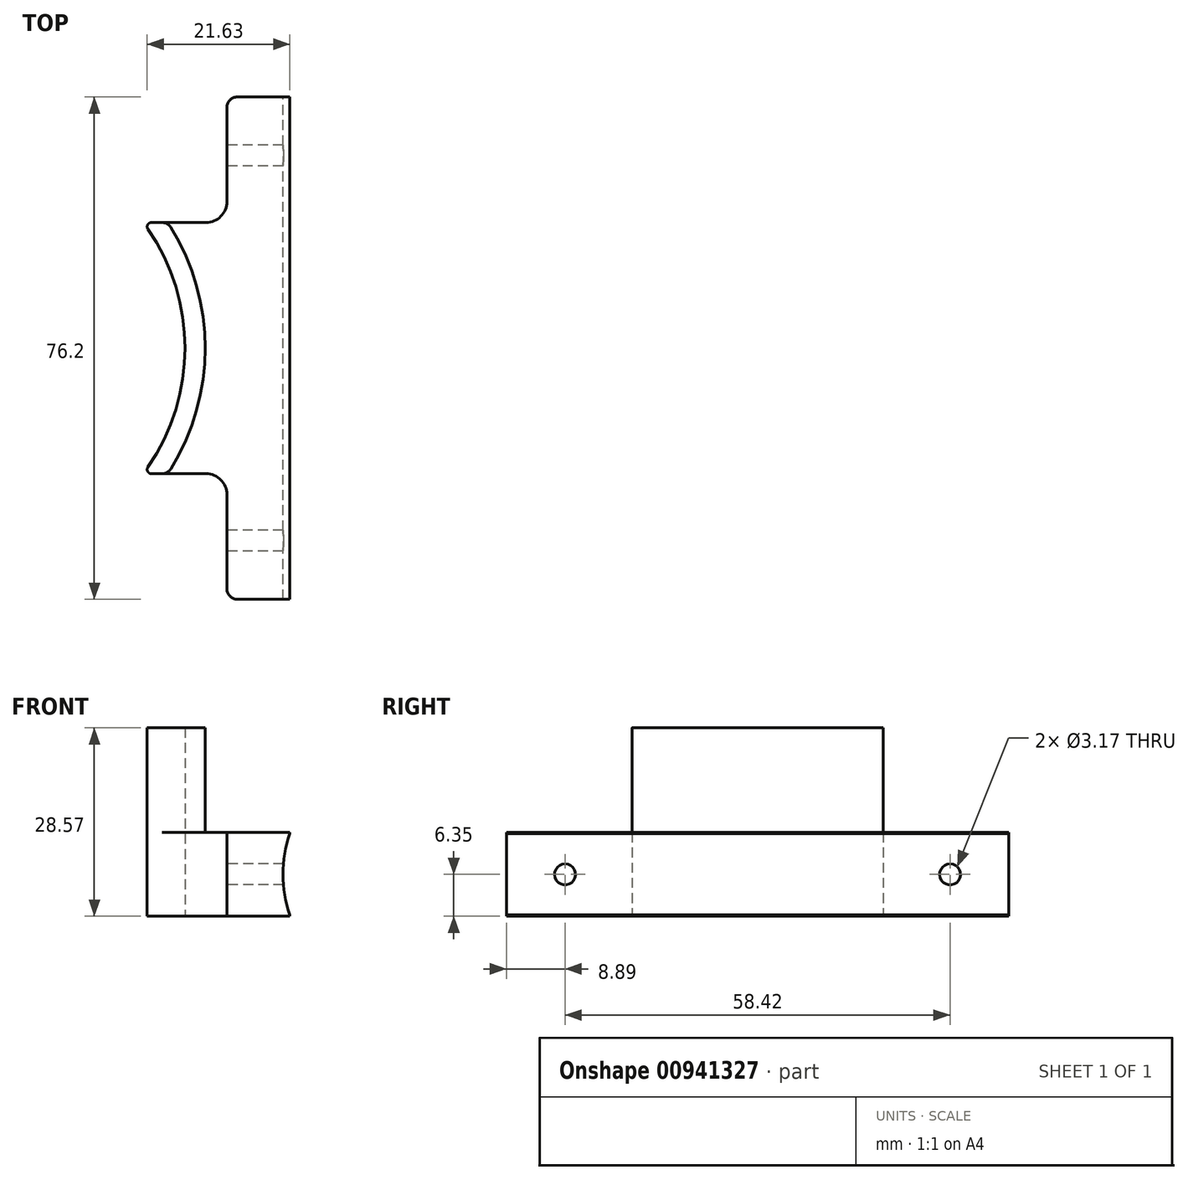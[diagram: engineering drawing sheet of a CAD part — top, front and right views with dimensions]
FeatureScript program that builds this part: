
annotation { "Feature Type Name" : "Feature", "Feature Type Description" : "" }
export const myFeature = defineFeature(function(context is Context, id is Id, definition is map)
    precondition{}
    {
        {
            var Q0;
            Q0=qCreatedBy(makeId("Top.planeOp"),FACE);
            var sketch = newSketch(context, id + "F0", { "sketchPlane" : qUnion([Q0])});
            skArc(sketch, "E0", {"start": v(26.12, -18.06) * mm, "mid": v(31.75, 0) * mm, "end": v(26.12, 18.06) * mm});
            skLineSegment(sketch, "E1", {"start": v(38.1, 25.4) * mm, "end": v(38.1, 36.51) * mm});
            skLineSegment(sketch, "E2", {"start": v(38.1, -25.4) * mm, "end": v(38.1, -36.51) * mm});
            skArc(sketch, "E3.0", {"start": v(29.12, -19.05) * mm, "mid": v(34.8, 0) * mm, "end": v(29.12, 19.05) * mm});
            skLineSegment(sketch, "E4", {"start": v(39.69, -38.1) * mm, "end": v(47.63, -38.1) * mm});
            skLineSegment(sketch, "E5", {"start": v(39.69, 38.1) * mm, "end": v(47.62, 38.1) * mm});
            skLineSegment(sketch, "E6", {"start": v(47.62, 38.1) * mm, "end": v(47.63, -38.1) * mm});
            skLineSegment(sketch, "E7", {"start": v(31.75, 19.05) * mm, "end": v(26.64, 19.05) * mm});
            skLineSegment(sketch, "E8", {"start": v(31.75, -19.05) * mm, "end": v(26.64, -19.05) * mm});
            skPoint(sketch, "E9.orphan", {"position": v(0, 31.75) * mm});
            skPoint(sketch, "E10.visualSharp", {"position": v(25.4, -19.05) * mm});
            skArc(sketch, "E10.filletArc", {"start": v(26.12, -18.06) * mm, "mid": v(26.08, -18.71) * mm, "end": v(26.64, -19.05) * mm});
            skPoint(sketch, "E11.visualSharp", {"position": v(25.4, 19.05) * mm});
            skArc(sketch, "E11.filletArc", {"start": v(26.64, 19.05) * mm, "mid": v(26.08, 18.71) * mm, "end": v(26.12, 18.06) * mm});
            skPoint(sketch, "E12.visualSharp", {"position": v(38.1, 38.1) * mm});
            skArc(sketch, "E12.filletArc", {"start": v(39.69, 38.1) * mm, "mid": v(38.56, 37.64) * mm, "end": v(38.1, 36.51) * mm});
            skPoint(sketch, "E13.visualSharp", {"position": v(38.1, -38.1) * mm});
            skArc(sketch, "E13.filletArc", {"start": v(38.1, -36.51) * mm, "mid": v(38.56, -37.64) * mm, "end": v(39.69, -38.1) * mm});
            skLineSegment(sketch, "E14", {"start": v(31.75, 19.05) * mm, "end": v(34.93, 19.05) * mm});
            skLineSegment(sketch, "E15", {"start": v(38.1, 25.4) * mm, "end": v(38.1, 22.22) * mm});
            skArc(sketch, "E16.filletArc", {"start": v(34.93, 19.05) * mm, "mid": v(37.17, 19.98) * mm, "end": v(38.1, 22.22) * mm});
            skLineSegment(sketch, "E17", {"start": v(31.75, -19.05) * mm, "end": v(34.93, -19.05) * mm});
            skLineSegment(sketch, "E18", {"start": v(38.1, -25.4) * mm, "end": v(38.1, -22.23) * mm});
            skArc(sketch, "E19.filletArc", {"start": v(38.1, -22.23) * mm, "mid": v(37.17, -19.98) * mm, "end": v(34.93, -19.05) * mm});
            skSolve(sketch);
        }
        {
            var Q0;
            Q0=makeQuery(id+"F0.imprint","IMPRINT",FACE,{"disambiguationData":[TD([[makeQuery(id+"F0.imprint","IMPRINT",EDGE,{"derivedFrom":sQuery(id+"F0.wireOp",EDGE,"E1")}),-1.0]])]});
            extrude(context, id + "F1", {"entities" : qUnion([Q0]), "depth" : 12.7 * mm, "offsetDistance" : 25.4 * mm});
        }
        {
            var Q0;
            Q0=qCreatedBy(makeId("Top.planeOp"),FACE);
            var sketch = newSketch(context, id + "F2", { "sketchPlane" : qUnion([Q0])});
            skArc(sketch, "E20", {"start": v(26.12, -18.06) * mm, "mid": v(31.75, 0) * mm, "end": v(26.12, 18.06) * mm});
            skPoint(sketch, "E21.0", {"position": v(29.12, 19.05) * mm});
            skPoint(sketch, "E22.0", {"position": v(29.12, -19.05) * mm});
            skLineSegment(sketch, "E23", {"start": v(29.12, 19.05) * mm, "end": v(26.64, 19.05) * mm});
            skLineSegment(sketch, "E24", {"start": v(29.12, -19.05) * mm, "end": v(26.64, -19.05) * mm});
            skArc(sketch, "E25.0", {"start": v(29.12, -19.05) * mm, "mid": v(34.8, 0) * mm, "end": v(29.12, 19.05) * mm});
            skPoint(sketch, "E26.visualSharp", {"position": v(25.4, 19.05) * mm});
            skArc(sketch, "E26.filletArc", {"start": v(26.64, 19.05) * mm, "mid": v(26.08, 18.71) * mm, "end": v(26.12, 18.06) * mm});
            skPoint(sketch, "E27.visualSharp", {"position": v(25.4, -19.05) * mm});
            skArc(sketch, "E27.filletArc", {"start": v(26.12, -18.06) * mm, "mid": v(26.08, -18.71) * mm, "end": v(26.64, -19.05) * mm});
            skSolve(sketch);
        }
        {
            var Q0;
            Q0=makeQuery(id+"F2.imprint","IMPRINT",FACE,{"disambiguationData":[TD([[makeQuery(id+"F2.imprint","IMPRINT",EDGE,{"derivedFrom":sQuery(id+"F2.wireOp",EDGE,"E20")}),-1.0]])]});
            extrude(context, id + "F3", {"entities" : qUnion([Q0]), "operationType" : NewBodyOperationType.ADD, "depth" : 28.57 * mm, "offsetDistance" : 25.4 * mm});
        }
        {
            var Q0;
            Q0=qCreatedBy(makeId("Right.planeOp"),FACE);
            var sketch = newSketch(context, id + "F4", { "sketchPlane" : qUnion([Q0])});
            skCircle(sketch, "E28", {"center": v(-29.21, 6.35) * mm, "radius": 1.59 * mm});
            skCircle(sketch, "E29", {"center": v(29.21, 6.35) * mm, "radius": 1.59 * mm});
            skSolve(sketch);
        }
        {
            var Q0;
            Q0=sQuery(id+"F4.wireOp",VERTEX,"E28.center");
            var Q1;
            Q1=makeQuery(id+"F1.opExtrude","SWEPT_BODY",BODY,{"disambiguationData":[OSD([sQuery(id+"F0.wireOp",EDGE,"E1"),sQuery(id+"F0.wireOp",EDGE,"E2"),sQuery(id+"F0.wireOp",EDGE,"E3.0"),sQuery(id+"F0.wireOp",EDGE,"E4"),sQuery(id+"F0.wireOp",EDGE,"E5"),sQuery(id+"F0.wireOp",EDGE,"E6"),sQuery(id+"F0.wireOp",EDGE,"E7"),sQuery(id+"F0.wireOp",EDGE,"E8"),sQuery(id+"F0.wireOp",EDGE,"76a3058a-905c-43c9-894b-0470b6126460.filletArc"),sQuery(id+"F0.wireOp",EDGE,"8e42873b-d39f-4a80-addc-4a2b4388c41b.filletArc")])]});
            hole(context, id + "F5", {"style" : HoleStyle.SIMPLE, "endStyle" : HoleEndStyle.THROUGH, "oppositeDirection" : true, "holeDiameter" : 3.17 * mm, "majorDiameter" : 6.35 * mm, "isTappedThrough" : true, "tappedDepth" : 12.7 * mm, "tapClearance" : 3, "locations" : qUnion([Q0]), "scope" : qUnion([Q1])});
        }
        {
            var Q0;
            Q0=sQuery(id+"F4.wireOp",VERTEX,"E29.center");
            var Q1;
            Q1=makeQuery(id+"F1.opExtrude","SWEPT_BODY",BODY,{"disambiguationData":[OSD([sQuery(id+"F0.wireOp",EDGE,"E1"),sQuery(id+"F0.wireOp",EDGE,"E2"),sQuery(id+"F0.wireOp",EDGE,"E3.0"),sQuery(id+"F0.wireOp",EDGE,"E4"),sQuery(id+"F0.wireOp",EDGE,"E5"),sQuery(id+"F0.wireOp",EDGE,"E6"),sQuery(id+"F0.wireOp",EDGE,"E7"),sQuery(id+"F0.wireOp",EDGE,"E8"),sQuery(id+"F0.wireOp",EDGE,"76a3058a-905c-43c9-894b-0470b6126460.filletArc"),sQuery(id+"F0.wireOp",EDGE,"8e42873b-d39f-4a80-addc-4a2b4388c41b.filletArc")])]});
            hole(context, id + "F6", {"style" : HoleStyle.SIMPLE, "endStyle" : HoleEndStyle.THROUGH, "oppositeDirection" : true, "holeDiameter" : 3.17 * mm, "majorDiameter" : 6.35 * mm, "isTappedThrough" : true, "tappedDepth" : 12.7 * mm, "tapClearance" : 3, "locations" : qUnion([Q0]), "scope" : qUnion([Q1])});
        }
        {
            var Q0;
            Q0=qCreatedBy(makeId("Front.planeOp"),FACE);
            var sketch = newSketch(context, id + "F7", { "sketchPlane" : qUnion([Q0])});
            skPoint(sketch, "E30.0", {"position": v(47.63, 6.35) * mm});
            skLineSegment(sketch, "E31", {"start": v(47.63, 6.35) * mm, "end": v(65.66, 6.35) * mm});
            skCircle(sketch, "E32", {"center": v(65.66, 6.35) * mm, "radius": 19.05 * mm});
            skSolve(sketch);
        }
        {
            var Q0;
            Q0=makeQuery(id+"F7.imprint","IMPRINT",FACE,{"disambiguationData":[TD([[makeQuery(id+"F7.imprint","IMPRINT",EDGE,{"derivedFrom":sQuery(id+"F7.wireOp",EDGE,"E32")}),1.0]])]});
            extrude(context, id + "F8", {"entities" : qUnion([Q0]), "operationType" : NewBodyOperationType.REMOVE, "depth" : 47 * mm, "offsetDistance" : 25.4 * mm, "hasSecondDirection" : true, "secondDirectionOppositeDirection" : true, "secondDirectionDepth" : 44.2 * mm});
        }
        {
            var Q0;
            Q0=makeQuery(id+"F3.opExtrude","SWEPT_EDGE",EDGE,{"disambiguationData":[OSD([sQuery(id+"F2.wireOp",EDGE,"E23"),sQuery(id+"F2.wireOp",EDGE,"E25.0")])]});
            fillet(context, id + "F9", {"entities" : qUnion([Q0]), "radius" : 1.52 * mm, "tangentPropagation" : true, "allowEdgeOverflow" : false});
        }
        {
            var Q0;
            Q0=makeQuery(id+"F3.opExtrude","SWEPT_EDGE",EDGE,{"disambiguationData":[OSD([sQuery(id+"F2.wireOp",EDGE,"E24"),sQuery(id+"F2.wireOp",EDGE,"E25.0")])]});
            fillet(context, id + "F10", {"entities" : qUnion([Q0]), "radius" : 1.52 * mm, "tangentPropagation" : true, "allowEdgeOverflow" : false});
        }
    });
